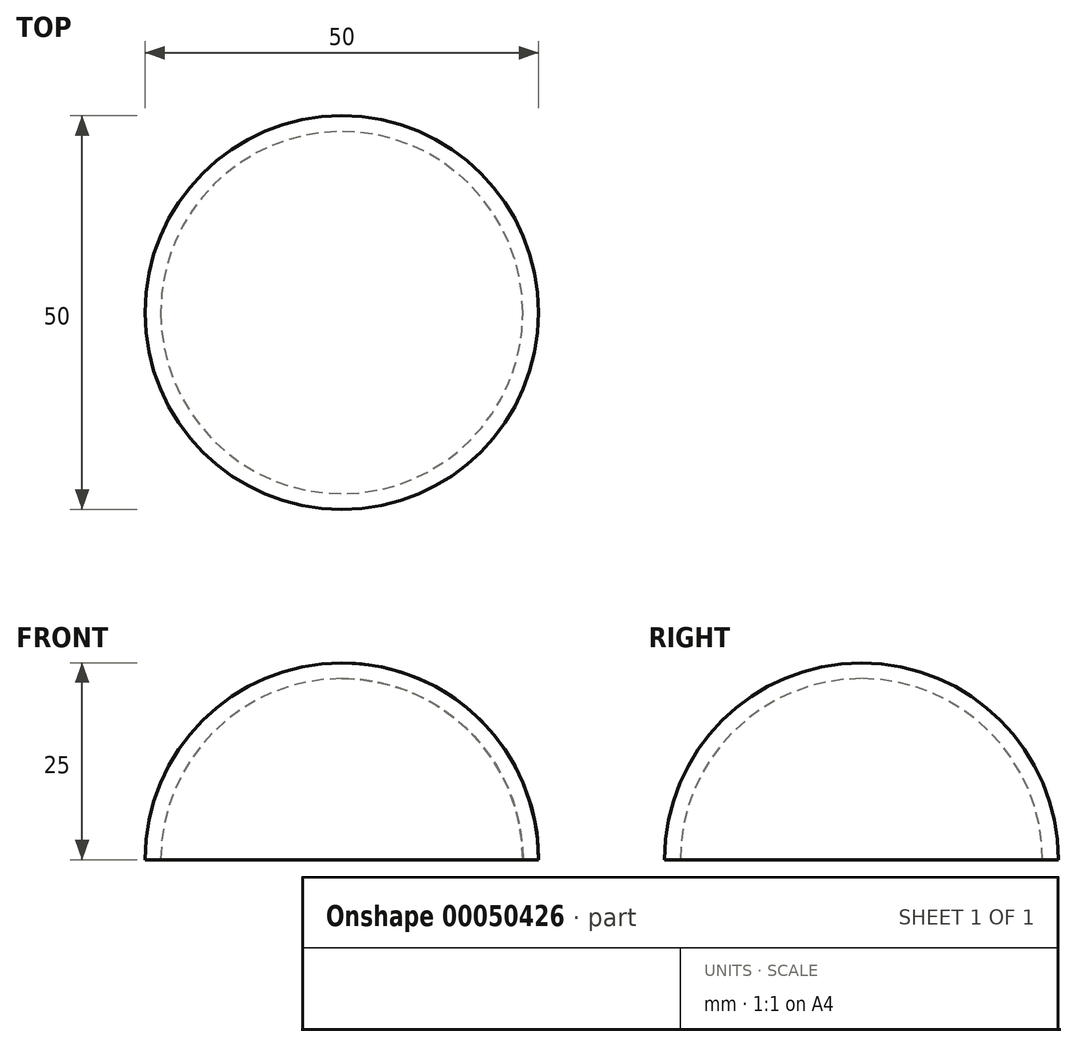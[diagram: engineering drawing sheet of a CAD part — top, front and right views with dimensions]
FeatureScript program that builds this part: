
annotation { "Feature Type Name" : "Feature", "Feature Type Description" : "" }
export const myFeature = defineFeature(function(context is Context, id is Id, definition is map)
    precondition{}
    {
        {
            var Q0;
            Q0=qCreatedBy(makeId("Front.planeOp"),FACE);
            var sketch = newSketch(context, id + "F0", { "sketchPlane" : qUnion([Q0])});
            skArc(sketch, "E0", {"start": v(25, 0) * mm, "mid": v(17.68, 17.68) * mm, "end": v(0, 25) * mm});
            skArc(sketch, "E1.0", {"start": v(23, 0) * mm, "mid": v(16.26, 16.26) * mm, "end": v(0, 23) * mm});
            skLineSegment(sketch, "E2", {"start": v(0, 25) * mm, "end": v(0, 23) * mm});
            skLineSegment(sketch, "E3", {"start": v(23, 0) * mm, "end": v(25, 0) * mm});
            skPoint(sketch, "E4.orphan", {"position": v(-25, 0) * mm});
            skLineSegment(sketch, "E5", {"start": v(0, 0) * mm, "end": v(0, 47.1) * mm, "construction": true});
            skSolve(sketch);
        }
        {
            var Q0;
            Q0 = qSketchRegion(id + "F0", true);
            var Q1;
            Q1=sQuery(id+"F0.wireOp",EDGE,"E5");
            revolve(context, id + "F1", {"entities" : qUnion([Q0]), "axis" : qUnion([Q1]), "revolveType" : RevolveType.FULL});
        }
    });
